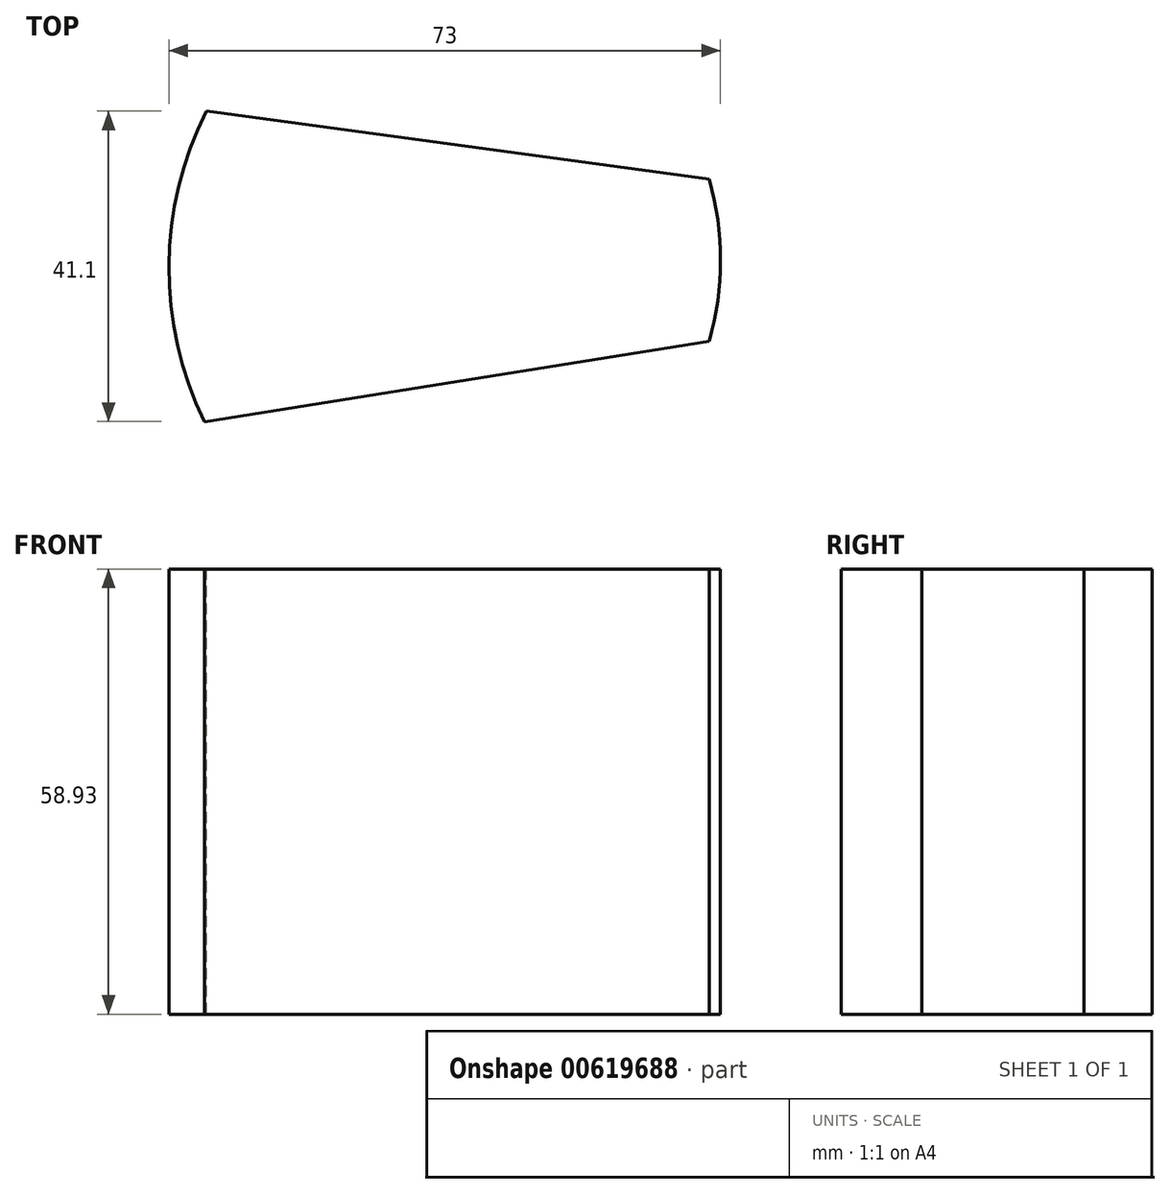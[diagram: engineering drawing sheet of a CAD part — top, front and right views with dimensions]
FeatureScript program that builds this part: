
annotation { "Feature Type Name" : "Feature", "Feature Type Description" : "" }
export const myFeature = defineFeature(function(context is Context, id is Id, definition is map)
    precondition{}
    {
        {
            var Q0;
            Q0=qCreatedBy(makeId("Top.planeOp"),FACE);
            var sketch = newSketch(context, id + "F0", { "sketchPlane" : qUnion([Q0])});
            skArc(sketch, "E0", {"start": v(-31.26, 19.56) * mm, "mid": v(-36.24, -0.96) * mm, "end": v(-31.56, -21.54) * mm});
            skLineSegment(sketch, "E1", {"start": v(-31.26, 19.56) * mm, "end": v(35.26, 10.55) * mm});
            skArc(sketch, "E2", {"start": v(35.26, -10.92) * mm, "mid": v(36.76, -0.19) * mm, "end": v(35.26, 10.55) * mm});
            skLineSegment(sketch, "E3", {"start": v(-31.56, -21.54) * mm, "end": v(35.26, -10.92) * mm});
            skSolve(sketch);
        }
        {
            var Q0;
            Q0 = qSketchRegion(id + "F0", true);
            extrude(context, id + "F1", {"entities" : qUnion([Q0]), "oppositeDirection" : true, "depth" : 58.93 * mm, "offsetDistance" : 25.4 * mm});
        }
    });
